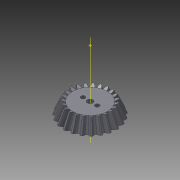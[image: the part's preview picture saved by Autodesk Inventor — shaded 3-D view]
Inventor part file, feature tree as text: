
AUTODESK INVENTOR PART (.ipt)
format: ipt  version: 2014 (Build 180170000, 170)  size: 648,192 bytes
history: native  units: mm
features: other x24, sketch x4, extrude x3, loft x2, pattern_circular x2, chamfer x1
ambient origin geometry x6: Origin, XZ Plane, X Axis, Y Axis, Z Axis, Center Point
bodies: Solid1 (feature_tree)
feature tree (36):
  other  "Top Point"
  other  "Mesh Plane2"
  other  "Teeth Body"
  other  "Start Point"
  other  "Tooth Plane"
  other  "Start Sketch"
  other  "End Point"
  other  "3D Sketch Right"
  other  "End Plane Right"
  loft  "Loft Right"
  pattern_circular  "Circular Pattern Right"  Count=2  [1 undecoded]
  other  "3D Sketch Left"
  other  "End Plane Left"
  loft  "Loft Left"
  pattern_circular  "Circular Pattern Left"  [2 undecoded]
  other  "Fix Body"
  extrude  "Extrusion1"  Depth=5.0mm
  extrude  "Extrusion2"  Depth=5.0mm
  chamfer  "Chamfer1"  Distance=10.724893mm
  extrude  "Extrusion3"  Depth=5.0mm
  other  "Mesh Plane"
  other  "Top Plane"
  other  "Teeth Body Sketch"
  other  "End Plane"
  other  "End Sketch"
  other  "Helical Curve Left"
  other  "End Sketch Left"
  other  "Body Sketch"
  sketch  "Sketch6"  dims[d0=69.0mm d1=62.323077mm]
  other  "Srf1"
  other  "Helical Curve Right"
  other  "End Sketch Right"
  sketch  "Sketch8"  dims[d2=74.564103mm d3=20.0mm]
  sketch  "Sketch9"  dims[d4=84.377418mm d5=90.0deg]
  sketch  "Sketch10"  dims[d7=13.741113mm d8=14.921461mm d9=31.50969mm d11=20.33mm d12=10.724893mm d15=11.64615mm d16=24.593208mm d17=0.0mm d18=90.0deg d19=0.0mm d20=90.0deg d21=230.0mm d22=360.0deg d26=676.499423mm d27=18.853034mm d28=69.0mm d29=-3.835275mm d30=10.724893mm d31=11.64615mm d32=24.593208mm d35=0.0mm d37=0.0mm d39=0.0mm d40=90.0deg d41=230.0mm d42=360.0deg d46=90.0deg d47=90.0deg d48=0.0mm d49=0.0mm d50=90.0deg d51=1.36591mm d52=0.0mm d53=0.0mm d54=0.0mm d56=27.073918mm d57=42.182765mm d58=32.810765mm d59=32.923508mm d60=25.608693mm d61=32.923508mm d62=25.608693mm d65=676.499423mm d66=31.5mm d67=69.0mm d68=-3.835275mm d69=18.853034mm d70=11.64615mm d71=24.593208mm d72=10.724893mm d73=25.608693mm d74=32.923508mm d75=0.0mm d77=0.0mm d79=0.0mm d80=90.0deg d81=230.0mm d82=360.0deg d84=10.0mm d85=20.0mm d86=20.0mm d87=10.0mm d88=0.0mm d89=0.0mm d90=90.0deg d91=90.0deg d92=90.0deg d93=90.0deg d94=8.0mm d95=10.0mm d96=0.0mm d97=20.0mm d98=6.0mm d99=10.0mm d100=0.0mm d101=3.0mm d102=10.0mm d103=45.0deg d104=10.1mm d105=5.0mm d106=0.0mm]
  other  "Pitch Diameter"
note: 3 required parameter values undecoded (feature->parameter linkage not recoverable at this tier; creation-order binding heuristic only, values carry confidence <= 0.55)
